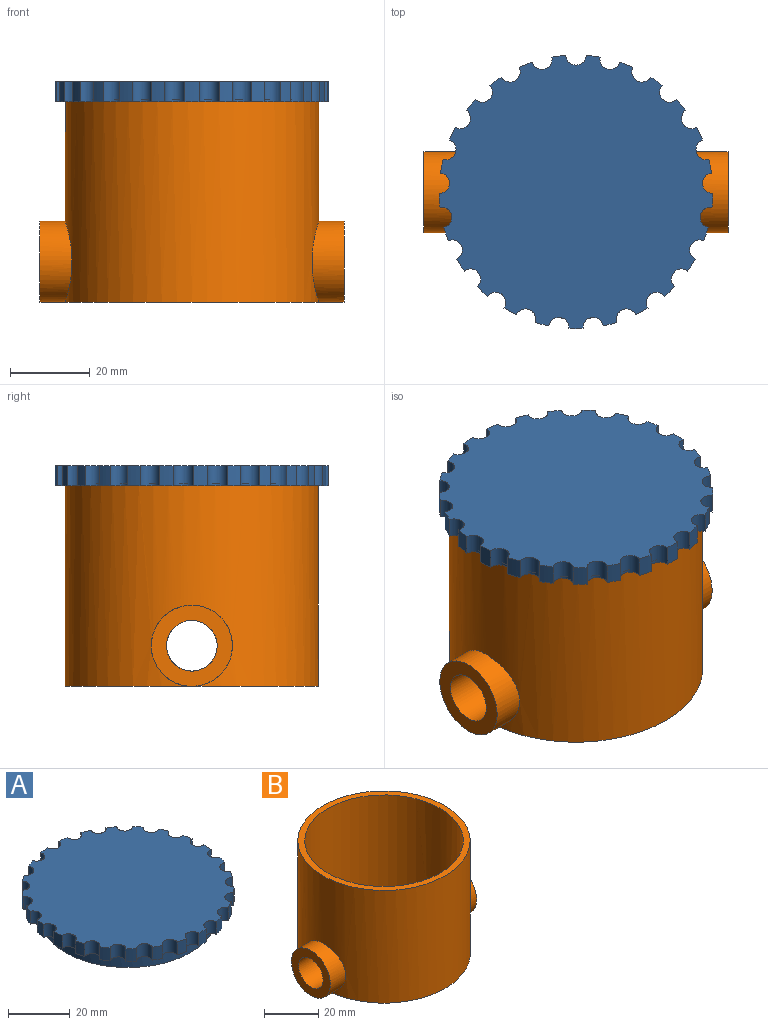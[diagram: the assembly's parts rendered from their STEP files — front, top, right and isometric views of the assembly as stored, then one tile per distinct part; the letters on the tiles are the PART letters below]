
ASSEMBLY  parts=2 mates=1
PART A: 56 faces, bbox 68.6x68.5x11.4 mm
  f0: cylinder r=2.54mm len=5.08mm, axis (0,0,-1), area 39.6mm2, adj f1,f49,f50,f51
  f1: cylinder r=34.29mm len=5.08mm, axis (0,0,-1), area 18mm2, adj f0,f2,f50,f51
  f2: cylinder r=2.54mm len=5.08mm, axis (0,0,-1), area 39.6mm2, adj f1,f3,f50,f51
  f3: cylinder r=34.29mm len=5.08mm, axis (0,0,-1), area 18mm2, adj f2,f4,f50,f51
  f4: cylinder r=2.54mm len=5.08mm, axis (0,0,-1), area 39.6mm2, adj f3,f5,f50,f51
  f5: cylinder r=34.29mm len=5.08mm, axis (0,0,-1), area 18mm2, adj f4,f6,f50,f51
  f6: cylinder r=2.54mm len=5.08mm, axis (0,0,-1), area 39.6mm2, adj f5,f7,f50,f51
  f7: cylinder r=34.29mm len=5.08mm, axis (0,0,-1), area 18mm2, adj f6,f8,f50,f51
  f8: cylinder r=2.54mm len=5.08mm, axis (0,0,-1), area 39.6mm2, adj f7,f9,f50,f51
  f9: cylinder r=34.29mm len=5.08mm, axis (0,0,-1), area 18mm2, adj f8,f10,f50,f51
  f10: cylinder r=2.54mm len=5.08mm, axis (0,0,-1), area 39.6mm2, adj f9,f11,f50,f51
  f11: cylinder r=34.29mm len=5.08mm, axis (0,0,-1), area 18mm2, adj f10,f12,f50,f51
  f12: cylinder r=2.54mm len=5.08mm, axis (0,0,-1), area 39.6mm2, adj f11,f13,f50,f51
  f13: cylinder r=34.29mm len=5.08mm, axis (0,0,-1), area 18mm2, adj f12,f14,f50,f51
  f14: cylinder r=2.54mm len=5.08mm, axis (0,0,-1), area 39.6mm2, adj f13,f15,f50,f51
  f15: cylinder r=34.29mm len=5.08mm, axis (0,0,-1), area 18mm2, adj f14,f16,f50,f51
  f16: cylinder r=2.54mm len=5.08mm, axis (0,0,-1), area 39.6mm2, adj f15,f17,f50,f51
  f17: cylinder r=34.29mm len=5.08mm, axis (0,0,-1), area 18mm2, adj f16,f18,f50,f51
  f18: cylinder r=2.54mm len=5.08mm, axis (0,0,-1), area 39.6mm2, adj f17,f19,f50,f51
  f19: cylinder r=34.29mm len=5.08mm, axis (0,0,-1), area 18mm2, adj f18,f20,f50,f51
  f20: cylinder r=2.54mm len=5.08mm, axis (0,0,-1), area 39.6mm2, adj f19,f21,f50,f51
  f21: cylinder r=34.29mm len=5.08mm, axis (0,0,-1), area 18mm2, adj f20,f22,f50,f51
  f22: cylinder r=2.54mm len=5.08mm, axis (0,0,-1), area 39.6mm2, adj f21,f23,f50,f51
  f23: cylinder r=34.29mm len=5.08mm, axis (0,0,-1), area 18mm2, adj f22,f24,f50,f51
  f24: cylinder r=2.54mm len=5.08mm, axis (0,0,-1), area 39.6mm2, adj f23,f25,f50,f51
  f25: cylinder r=34.29mm len=5.08mm, axis (0,0,-1), area 18mm2, adj f24,f26,f50,f51
  f26: cylinder r=2.54mm len=5.08mm, axis (0,0,-1), area 39.6mm2, adj f25,f27,f50,f51
  f27: cylinder r=34.29mm len=5.08mm, axis (0,0,-1), area 18mm2, adj f26,f28,f50,f51
  f28: cylinder r=2.54mm len=5.08mm, axis (0,0,-1), area 39.6mm2, adj f27,f29,f50,f51
  f29: cylinder r=34.29mm len=5.08mm, axis (0,0,-1), area 18mm2, adj f28,f30,f50,f51
  f30: cylinder r=2.54mm len=5.08mm, axis (0,0,-1), area 39.6mm2, adj f29,f31,f50,f51
  f31: cylinder r=34.29mm len=5.08mm, axis (0,0,-1), area 18mm2, adj f30,f32,f50,f51
  f32: cylinder r=2.54mm len=5.08mm, axis (0,0,-1), area 39.6mm2, adj f31,f33,f50,f51
  f33: cylinder r=34.29mm len=5.08mm, axis (0,0,-1), area 18mm2, adj f32,f34,f50,f51
  f34: cylinder r=2.54mm len=5.08mm, axis (0,0,-1), area 39.6mm2, adj f33,f35,f50,f51
  f35: cylinder r=34.29mm len=5.08mm, axis (0,0,-1), area 18mm2, adj f34,f36,f50,f51
  f36: cylinder r=2.54mm len=5.08mm, axis (0,0,-1), area 39.6mm2, adj f35,f37,f50,f51
  f37: cylinder r=34.29mm len=5.08mm, axis (0,0,-1), area 18mm2, adj f36,f38,f50,f51
  f38: cylinder r=2.54mm len=5.08mm, axis (0,0,-1), area 39.6mm2, adj f37,f39,f50,f51
  f39: cylinder r=34.29mm len=5.08mm, axis (0,0,-1), area 18mm2, adj f38,f40,f50,f51
  f40: cylinder r=2.54mm len=5.08mm, axis (0,0,-1), area 39.6mm2, adj f39,f41,f50,f51
  f41: cylinder r=34.29mm len=5.08mm, axis (0,0,-1), area 18mm2, adj f40,f42,f50,f51
  f42: cylinder r=2.54mm len=5.08mm, axis (0,0,-1), area 39.6mm2, adj f41,f43,f50,f51
  f43: cylinder r=34.29mm len=5.08mm, axis (0,0,-1), area 18mm2, adj f42,f44,f50,f51
  f44: cylinder r=2.54mm len=5.08mm, axis (0,0,-1), area 39.6mm2, adj f43,f45,f50,f51
  f45: cylinder r=34.29mm len=5.08mm, axis (0,0,-1), area 18mm2, adj f44,f46,f50,f51
  f46: cylinder r=2.54mm len=5.08mm, axis (0,0,-1), area 39.6mm2, adj f45,f47,f50,f51
  f47: cylinder r=34.29mm len=5.08mm, axis (0,0,-1), area 18mm2, adj f46,f48,f50,f51
  f48: cylinder r=2.54mm len=5.08mm, axis (0,0,-1), area 39.6mm2, adj f47,f49,f50,f51
  f49: cylinder r=34.29mm len=5.08mm, axis (0,0,-1), area 18mm2, adj f0,f48,f50,f51
  f50: plane 68.58x68.49mm, normal (0,0,1), area 3444.5mm2, adj f0,f1,f2,f3,f4,f5,f6,f7
  f51: plane 68.58x68.49mm, normal (0,0,-1), area 879.3mm2, adj f0,f1,f2,f3,f4,f5,f6,f7
  f52: cylinder r=27.3mm len=54.61mm, axis (0,0,1), area 1089.4mm2, adj f54,f55
  f53: cylinder r=28.57mm len=57.15mm, axis (0,0,1), area 1140.1mm2, adj f51,f54
  f54: plane 57.15x57.15mm, normal (0,0,-1), area 223mm2, adj f52,f53
  f55: plane 54.61x54.61mm, normal (0,0,-1), area 2342.3mm2, adj f52
PART B: 11 faces, bbox 76.2x63.5x50.8 mm
  f0: cylinder r=6.35mm len=12.7mm, axis (-1,0,0), area 368.6mm2, adj f4,f9
  f1: cylinder r=31.75mm len=63.5mm, axis (0,0,-1), area 9477.2mm2, adj f2,f3,f5,f6
  f2: plane 63.5x63.5mm, normal (0,0,1), area 486.4mm2, adj f1,f9
  f3: plane 63.5x63.5mm, normal (0,0,-1), area 3166.9mm2, adj f1
  f4: plane 20.32x20.32mm, normal (1,0,0), area 197.6mm2, adj f0,f5
  f5: cylinder r=10.16mm len=20.32mm, axis (-1,0,0), area 458.3mm2, adj f1,f4
  f6: cylinder r=10.16mm len=20.32mm, axis (-1,0,0), area 458.3mm2, adj f1,f7
  f7: plane 20.32x20.32mm, normal (-1,0,0), area 197.6mm2, adj f6,f8
  f8: cylinder r=6.35mm len=12.7mm, axis (-1,0,0), area 368.6mm2, adj f7,f9
  f9: cylinder r=29.21mm len=58.42mm, axis (0,0,1), area 8603mm2, adj f0,f2,f8,f10
  f10: plane 58.42x58.42mm, normal (0,0,1), area 2680.5mm2, adj f9
PLACE A t=(-28.64,-16.06,42.12)mm
PLACE B t=(-28.64,-16.06,-8.08)mm
MATE cylindrical A.f53 <-> B.f9  axis (0,0,1) through (-28.64,-16.06,38.94)mm
